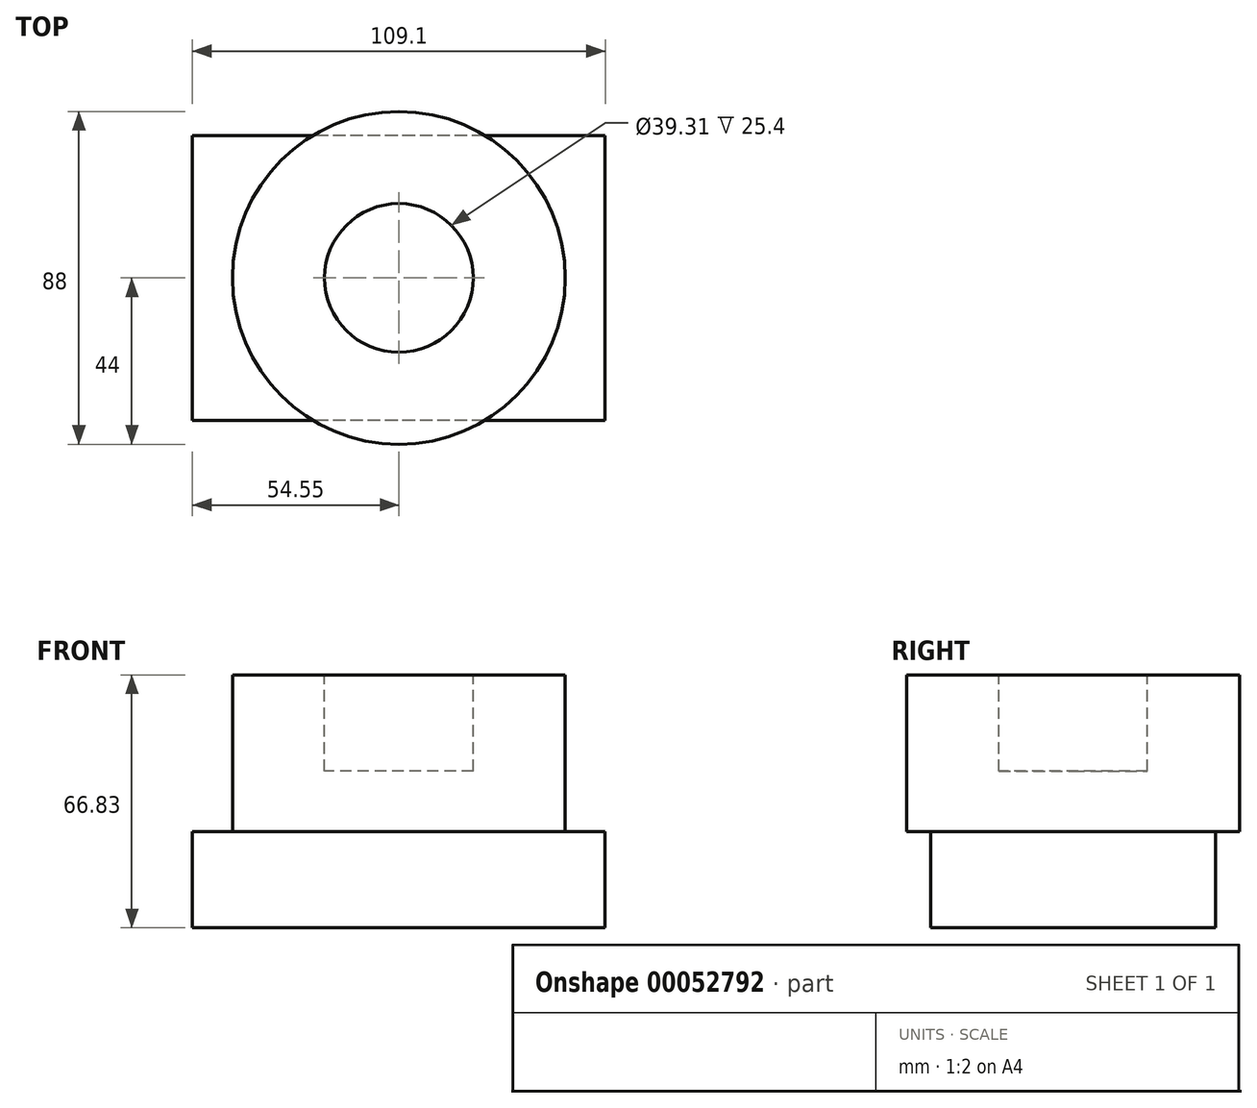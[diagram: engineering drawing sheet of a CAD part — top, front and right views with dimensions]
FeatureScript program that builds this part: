
annotation { "Feature Type Name" : "Feature", "Feature Type Description" : "" }
export const myFeature = defineFeature(function(context is Context, id is Id, definition is map)
    precondition{}
    {
        {
            var Q0;
            Q0=qCreatedBy(makeId("Top.planeOp"),FACE);
            var sketch = newSketch(context, id + "F0", { "sketchPlane" : qUnion([Q0])});
            skLineSegment(sketch, "E0.rect.bottom", {"start": v(54.55, -37.69) * mm, "end": v(-54.55, -37.69) * mm});
            skLineSegment(sketch, "E0.rect.top", {"start": v(54.55, 37.69) * mm, "end": v(-54.55, 37.69) * mm});
            skLineSegment(sketch, "E0.rect.left", {"start": v(54.55, -37.69) * mm, "end": v(54.55, 37.69) * mm});
            skLineSegment(sketch, "E0.rect.right", {"start": v(-54.55, -37.69) * mm, "end": v(-54.55, 37.69) * mm});
            skPoint(sketch, "E0.rect.middle", {"position": v(0, 0) * mm});
            skSolve(sketch);
        }
        {
            var Q0;
            Q0 = qSketchRegion(id + "F0", true);
            extrude(context, id + "F1", {"entities" : qUnion([Q0]), "depth" : 25.4 * mm});
        }
        {
            var Q0;
            Q0=qCreatedBy(makeId("Front.planeOp"),FACE);
            var sketch = newSketch(context, id + "F2", { "sketchPlane" : qUnion([Q0])});
            skLineSegment(sketch, "E1", {"start": v(0, 25.75) * mm, "end": v(0, 66.83) * mm, "construction": true});
            skLineSegment(sketch, "E2", {"start": v(0, 66.83) * mm, "end": v(-44, 66.83) * mm});
            skLineSegment(sketch, "E3", {"start": v(-44, 66.83) * mm, "end": v(-44, 25.4) * mm});
            skLineSegment(sketch, "E4", {"start": v(-44, 25.4) * mm, "end": v(0, 25.4) * mm});
            skLineSegment(sketch, "E5", {"start": v(0, 66.83) * mm, "end": v(0, 25.4) * mm});
            skSolve(sketch);
        }
        {
            var Q0;
            Q0 = qSketchRegion(id + "F2", true);
            var Q1;
            Q1=sQuery(id+"F2.wireOp",EDGE,"E5");
            revolve(context, id + "F3", {"operationType" : NewBodyOperationType.ADD, "entities" : qUnion([Q0]), "axis" : qUnion([Q1]), "revolveType" : RevolveType.FULL});
        }
        {
            var Q0;
            Q0=makeQuery(id+"F3.opRevolve","SWEPT_FACE",FACE,{"disambiguationData":[OSD([sQuery(id+"F2.wireOp",EDGE,"E2")])]});
            var sketch = newSketch(context, id + "F4", { "sketchPlane" : qUnion([Q0])});
            skCircle(sketch, "E6", {"center": v(0, 0) * mm, "radius": 19.66 * mm});
            skSolve(sketch);
        }
        {
            var Q0;
            Q0=makeQuery(id+"F4.imprint","IMPRINT",FACE,{"disambiguationData":[TD([[makeQuery(id+"F4.imprint","IMPRINT",EDGE,{"derivedFrom":sQuery(id+"F4.wireOp",EDGE,"E6")}),1.0]])]});
            extrude(context, id + "F5", {"entities" : qUnion([Q0]), "operationType" : NewBodyOperationType.REMOVE, "oppositeDirection" : true, "depth" : 25.4 * mm});
        }
    });
